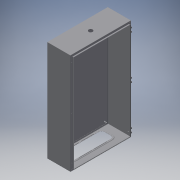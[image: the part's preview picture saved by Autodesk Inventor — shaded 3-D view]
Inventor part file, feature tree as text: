
AUTODESK INVENTOR PART (.ipt)
format: ipt  version: 2017 (Build 210142000, 142)  size: 1,788,416 bytes
history: native  units: in
note: dims shown in document units (in); Inventor stores cm internally (conversion verified against a paired STEP export)
features: other x1, hole x1
ambient origin geometry x8: Origin, YZ Plane, XZ Plane, XY Plane, X Axis, Y Axis, Z Axis, Center Point
bodies: Solid1 (feature_tree)
feature tree (2):
  other  "nsycrn106250t"
  hole  "Hole1"  [1 undecoded]
note: 1 required parameter value undecoded (feature->parameter linkage not recoverable at this tier; creation-order binding heuristic only, values carry confidence <= 0.55)
